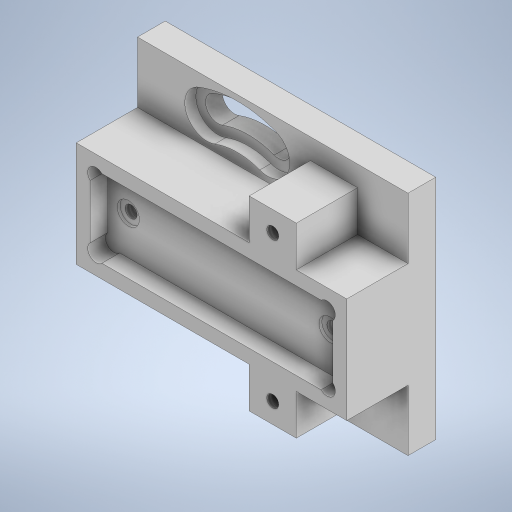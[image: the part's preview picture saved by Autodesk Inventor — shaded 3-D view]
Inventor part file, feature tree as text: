
AUTODESK INVENTOR PART (.ipt)
format: ipt  version: 2024.2 (Build 282272000, 272)  size: 514,560 bytes
history: native  units: in
note: dims shown in document units (in); Inventor stores cm internally (conversion verified against a paired STEP export)
features: extrude x11, hole x7, sketch x7, chamfer x1
ambient origin geometry x8: Origin, YZ Plane, XZ Plane, XY Plane, X Axis, Y Axis, Z Axis, Center Point
bodies: Solid1 (feature_tree)
feature tree (26):
  extrude  "Extrusion1"  TaperAngle=0.0deg  [1 undecoded]
  hole  "Hole1"  [1 undecoded]
  hole  "Hole2"  [1 undecoded]
  hole  "Hole3"  [1 undecoded]
  extrude  "Extrusion2"  Depth=0.0394in
  extrude  "Extrusion3"  TaperAngle=0.0deg  [1 undecoded]
  hole  "Hole5"  [1 undecoded]
  hole  "Hole6"  [1 undecoded]
  extrude  "Extrusion4"  Depth=0.0413in
  extrude  "Extrusion6"  Depth=0.0827in TaperAngle=0.0deg
  chamfer  "Chamfer5"  Distance=1.9213in
  sketch  "Sketch12"  dims[d2=0.5059in d3=0.0in]
  extrude  "Extrusion12"  Depth=1.6142in
  extrude  "Extrusion13"  Depth=0.1969in TaperAngle=0.0deg
  hole  "Hole7"  [1 undecoded]
  sketch  "Sketch15"  dims[d12=0.0in d13=1.4331in]
  sketch  "Sketch17"  dims[d14=0.7165in]
  extrude  "Extrusion14"  TaperAngle=0.0deg  [1 undecoded]
  extrude  "Extrusion15"  TaperAngle=0.0deg  [1 undecoded]
  extrude  "Extrusion16"  TaperAngle=0.0deg  [1 undecoded]
  extrude  "Extrusion17"  Depth=0.0197in
  hole  "Hole8"  [1 undecoded]
  sketch  "Sketch14"  dims[d4=0.0849in d5=0.224in d6=0.1575in d7=0.0787in d8=90.0deg d9=0.3492in d10=0.0in d11=0.0in]
  sketch  "Sketch19"  dims[d15=0.1772in d16=0.224in d17=0.315in d18=0.3445in d19=0.5635in d20=0.3492in d21=0.0in d22=0.0in]
  sketch  "Sketch20"  dims[d23=0.0in d24=0.0394in]
  sketch  "Sketch21"  dims[d25=0.0in d26=0.0in d27=0.3937in d28=0.1969in d29=0.0413in d30=0.0827in d31=0.224in d32=0.315in d33=0.1654in d34=0.5635in d35=0.0827in d36=0.0in d37=0.0827in d38=0.0in d39=1.9213in d40=1.6142in d41=0.1969in d42=0.0in d54=0.0in d55=0.0in d56=0.0in d57=0.0in d58=0.1575in d59=0.224in d60=0.315in d61=0.0787in d62=0.5635in d63=0.0197in d64=0.0in d77=0.0394in d78=0.0413in d79=0.3937in d80=0.0in d81=0.0in d82=0.1969in d83=0.0827in d84=0.224in d85=0.315in d86=0.0787in d87=0.5635in d88=0.0827in d89=0.0in d90=0.0827in d91=0.0in d97=1.9213in d98=0.748in d99=1.7244in d100=0.5512in d101=0.126in d102=0.0in d103=0.0394in d104=0.0787in d105=45.0deg d106=0.1181in d107=45.0deg d108=45.0deg d109=45.0deg d110=0.1181in d111=0.1181in d112=0.1181in d118=0.315in d122=0.1772in d129=0.0in d130=0.0in d131=0.0787in d132=0.0in d133=0.0827in d134=0.2362in d135=0.1575in d136=0.0787in d137=90.0deg d138=0.0827in d139=0.0in d140=1.5354in d141=0.9055in d142=1.3976in d143=1.0433in d147=0.315in d148=0.1772in d149=0.1772in d150=0.315in d151=0.0in d152=0.0in d153=0.0787in d154=0.0in d155=0.3583in d156=0.3346in d157=0.2874in d158=0.435in d159=0.0in d160=0.3583in d161=0.3346in d162=0.2874in d163=0.435in d164=0.0in d165=0.1437in d166=0.0849in d167=0.224in d168=0.1575in d169=0.0787in d170=90.0deg d171=0.3492in d172=0.0in d127=0.0197in d128=0.0344in]
note: 12 required parameter values undecoded (feature->parameter linkage not recoverable at this tier; creation-order binding heuristic only, values carry confidence <= 0.55)
